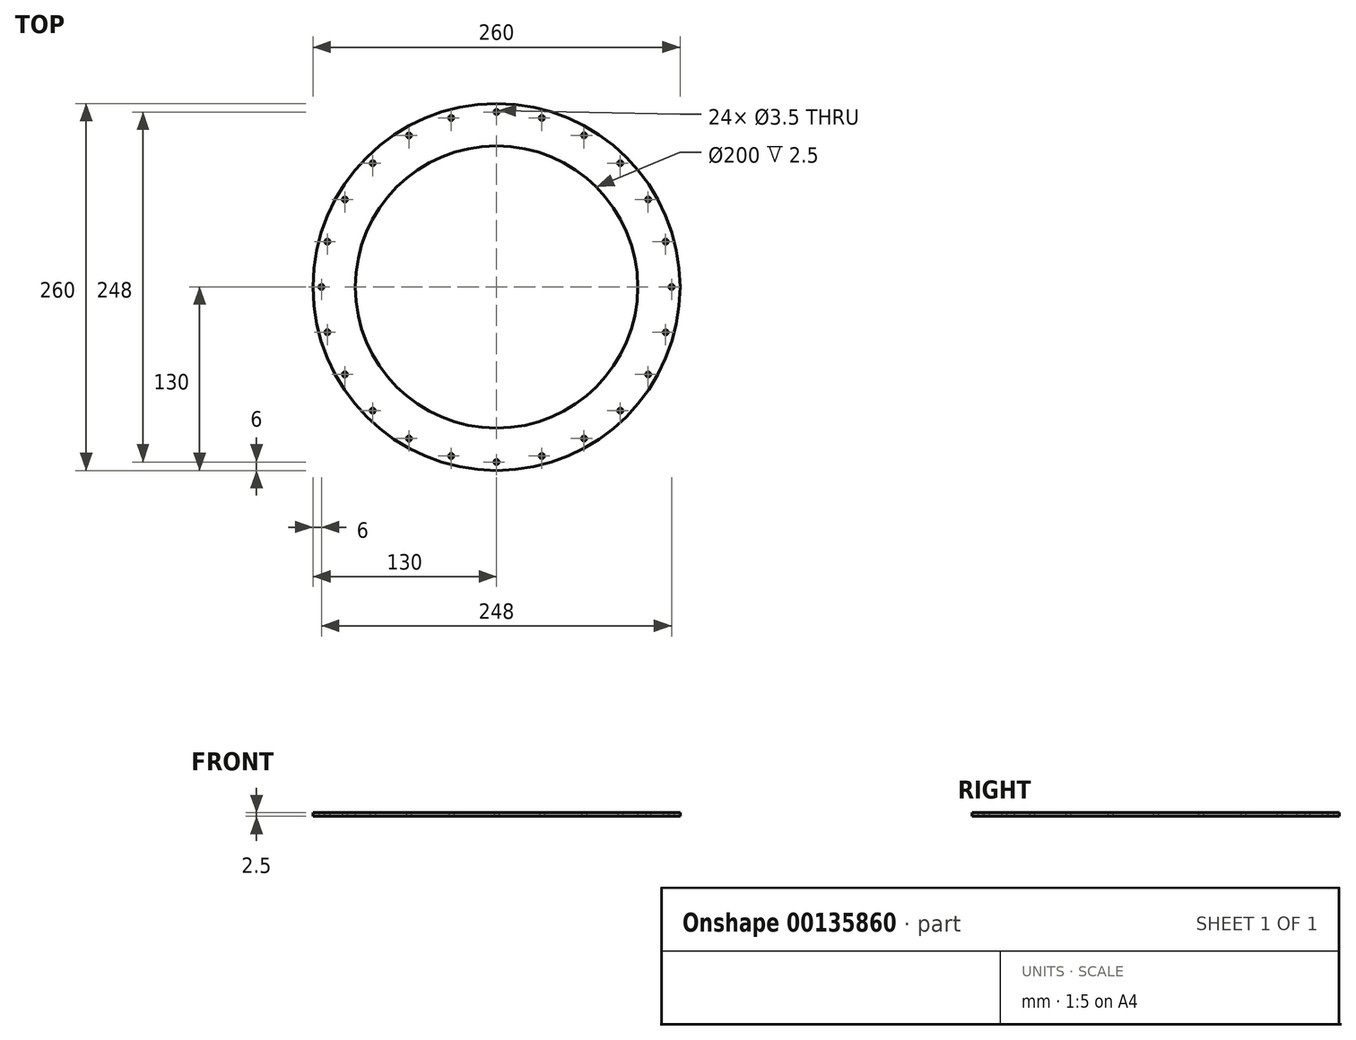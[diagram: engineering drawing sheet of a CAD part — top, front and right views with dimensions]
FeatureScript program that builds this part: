
annotation { "Feature Type Name" : "Feature", "Feature Type Description" : "" }
export const myFeature = defineFeature(function(context is Context, id is Id, definition is map)
    precondition{}
    {
        {
            var Q0;
            Q0=qCreatedBy(makeId("Top.planeOp"),FACE);
            var sketch = newSketch(context, id + "F0", { "sketchPlane" : qUnion([Q0])});
            skCircle(sketch, "E0", {"center": v(0, 0) * mm, "radius": 130 * mm});
            skCircle(sketch, "E1", {"center": v(0, 0) * mm, "radius": 100 * mm});
            skLineSegment(sketch, "E2", {"start": v(0, 0) * mm, "end": v(124, 0) * mm, "construction": true});
            skCircle(sketch, "E3", {"center": v(124, 0) * mm, "radius": 1.75 * mm});
            skCircle(sketch, "E4.1.0", {"center": v(119.77, 32.1) * mm, "radius": 1.75 * mm});
            skCircle(sketch, "E4.2.0", {"center": v(107.39, 62) * mm, "radius": 1.75 * mm});
            skCircle(sketch, "E4.3.0", {"center": v(87.68, 87.68) * mm, "radius": 1.75 * mm});
            skCircle(sketch, "E4.4.0", {"center": v(62, 107.39) * mm, "radius": 1.75 * mm});
            skCircle(sketch, "E4.5.0", {"center": v(32.1, 119.77) * mm, "radius": 1.75 * mm});
            skCircle(sketch, "E4.6.0", {"center": v(0, 124) * mm, "radius": 1.75 * mm});
            skCircle(sketch, "E4.7.0", {"center": v(-32.1, 119.77) * mm, "radius": 1.75 * mm});
            skCircle(sketch, "E4.8.0", {"center": v(-62, 107.39) * mm, "radius": 1.75 * mm});
            skCircle(sketch, "E4.9.0", {"center": v(-87.68, 87.68) * mm, "radius": 1.75 * mm});
            skCircle(sketch, "E4.10.0", {"center": v(-107.39, 62) * mm, "radius": 1.75 * mm});
            skCircle(sketch, "E4.11.0", {"center": v(-119.77, 32.1) * mm, "radius": 1.75 * mm});
            skCircle(sketch, "E4.12.0", {"center": v(-124, 0) * mm, "radius": 1.75 * mm});
            skCircle(sketch, "E4.13.0", {"center": v(-119.77, -32.1) * mm, "radius": 1.75 * mm});
            skCircle(sketch, "E4.14.0", {"center": v(-107.39, -62) * mm, "radius": 1.75 * mm});
            skCircle(sketch, "E4.15.0", {"center": v(-87.68, -87.68) * mm, "radius": 1.75 * mm});
            skCircle(sketch, "E4.16.0", {"center": v(-62, -107.39) * mm, "radius": 1.75 * mm});
            skCircle(sketch, "E4.17.0", {"center": v(-32.1, -119.77) * mm, "radius": 1.75 * mm});
            skCircle(sketch, "E4.18.0", {"center": v(0, -124) * mm, "radius": 1.75 * mm});
            skCircle(sketch, "E4.19.0", {"center": v(32.1, -119.77) * mm, "radius": 1.75 * mm});
            skCircle(sketch, "E4.20.0", {"center": v(62, -107.39) * mm, "radius": 1.75 * mm});
            skCircle(sketch, "E4.21.0", {"center": v(87.68, -87.68) * mm, "radius": 1.75 * mm});
            skCircle(sketch, "E4.22.0", {"center": v(107.39, -62) * mm, "radius": 1.75 * mm});
            skCircle(sketch, "E4.23.0", {"center": v(119.77, -32.1) * mm, "radius": 1.75 * mm});
            skSolve(sketch);
        }
        {
            var Q0;
            Q0=makeQuery(id+"F0.imprint","IMPRINT",FACE,{"disambiguationData":[TD([[makeQuery(id+"F0.imprint","IMPRINT",EDGE,{"derivedFrom":sQuery(id+"F0.wireOp",EDGE,"E0")}),1.0]])]});
            extrude(context, id + "F1", {"entities" : qUnion([Q0]), "depth" : 2.5 * mm});
        }
    });
